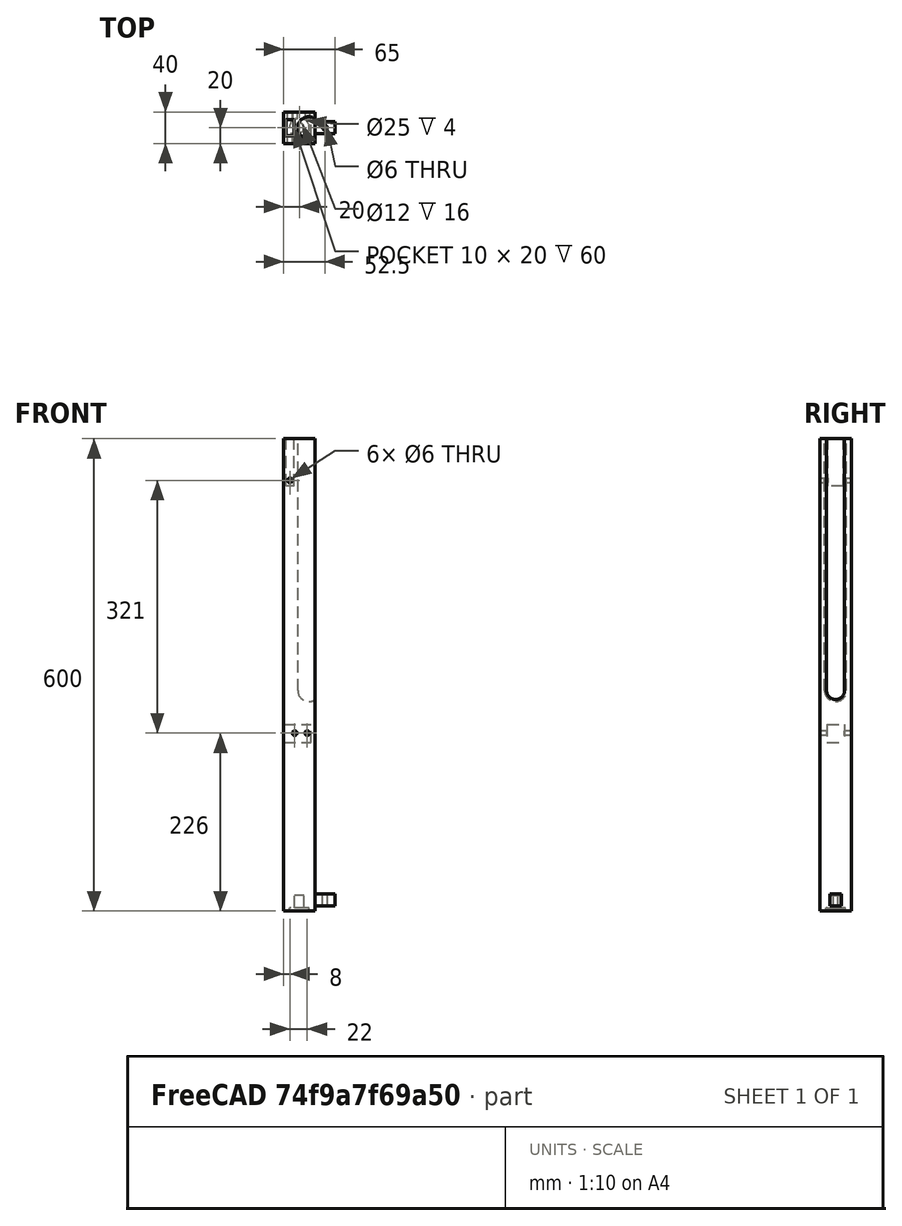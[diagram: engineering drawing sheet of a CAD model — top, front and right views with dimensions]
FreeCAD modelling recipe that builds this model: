
FCSTD DOCUMENT  (FreeCAD 0.16R6704 (Git))
Label: 2º barra grande 2
License: All rights reserved
LicenseURL: http://en.wikipedia.org/wiki/All_rights_reserved
objects: Part::Cut×10, Part::Cylinder×7, Part::Box×4, Part::Sphere×1, Part::MultiFuse×1
note: 23 computed .brp shape members not serialized (recipe doc carries the construction recipe); baked Part::Feature solids carry a one-line shape summary decoded from their .brp

FEATURE [Part::Box] Box115  label="Cub principal003"
  Height = 600
  Length = 40
  Placement = pos=(0,-20,-15) rot=(0,0,1;0rad)
  Width = 40
FEATURE [Part::Cylinder] Cylinder184  label="cilindro de seguridad003"
  Angle = 360
  Height = 320
  Placement = pos=(8,0,265) rot=(0,0,1;0rad)
  Radius = 14
FEATURE [Part::Box] Box116  label="Agujero del saliente003"
  Height = 60
  Length = 10
  Placement = pos=(27,-10,525) rot=(0,0,1;0rad)
  Width = 20
FEATURE [Part::Cylinder] Cylinder185  label="Pasador003"
  Angle = 360
  Height = 60
  Placement = pos=(32,30,532) rot=(1,0,0;1.5708rad)
  Radius = 3
FEATURE [Part::Cut] Cut230
  Base = -> Box115
  Tool = -> Cylinder184
FEATURE [Part::Cut] Cut231
  Base = -> Cut230
  Tool = -> Box116
FEATURE [Part::Cut] Cut232
  Base = -> Cut231
  Tool = -> Cylinder185
FEATURE [Part::Sphere] Sphere017  label="esfera de seguridad014"
  Angle1 = -90
  Angle2 = 90
  Angle3 = 360
  Placement = pos=(8,0,265) rot=(0,0,1;0rad)
  Radius = 14
FEATURE [Part::Cut] Cut233  label="2º pieza grande002"
  Base = -> Cut232
  Placement = pos=(-440,0,0) rot=(0,0,1;3.14159rad)
  Tool = -> Sphere017
FEATURE [Part::Box] Box117  label="Cubo079"
  Height = 15
  Length = 25
  Placement = pos=(-440,-7.5,-8.5) rot=(0,0,1;0rad)
  Width = 15
FEATURE [Part::Cylinder] Cylinder186  label="PASADOR007"
  Angle = 360
  Height = 16
  Placement = pos=(-460,0,-11) rot=(0,0,1;0rad)
  Radius = 6
FEATURE [Part::Cylinder] Cylinder187  label="rodamiento006"
  Angle = 360
  Height = 4
  Placement = pos=(-460,0,-15) rot=(0,0,1;0rad)
  Radius = 12.5
FEATURE [Part::Cut] Cut234
  Base = -> Cut233
  Tool = -> Cylinder187
FEATURE [Part::Cut] Cut235
  Base = -> Cut234
  Tool = -> Cylinder186
FEATURE [Part::Cylinder] Cylinder188  label="Cilindro105"
  Angle = 360
  Height = 65
  Placement = pos=(-427.5,0,-24.5) rot=(0,0,1;0rad)
  Radius = 3
FEATURE [Part::Cut] Cut236
  Base = -> Box117
  Tool = -> Cylinder188
FEATURE [Part::MultiFuse] Fusion057  label="Fusion060"
  Shapes = -> [Cut235,Cut236]
FEATURE [Part::Cylinder] Cylinder193  label="Agujero reposapies002"
  Angle = 360
  Height = 100
  Placement = pos=(-450,50,211) rot=(1,0,0;1.5708rad)
  Radius = 3
FEATURE [Part::Cut] Cut244  label="2º pieza grande003"
  Base = -> Fusion057
  Placement = pos=(0,460,0) rot=(0,0,1;0rad)
  Tool = -> Cylinder193
FEATURE [Part::Box] Box129  label="Cubo092"
  Height = 23
  Length = 60
  Placement = pos=(-505,449,199) rot=(0,0,1;0rad)
  Width = 22
FEATURE [Part::Cut] Cut284
  Base = -> Cut244
  Tool = -> Box129
FEATURE [Part::Cylinder] Cylinder265  label="Agujero reposapies004"
  Angle = 360
  Height = 50
  Placement = pos=(-466,485,211) rot=(1,0,0;1.5708rad)
  Radius = 3
FEATURE [Part::Cut] Cut285
  Base = -> Cut284
  Tool = -> Cylinder265
